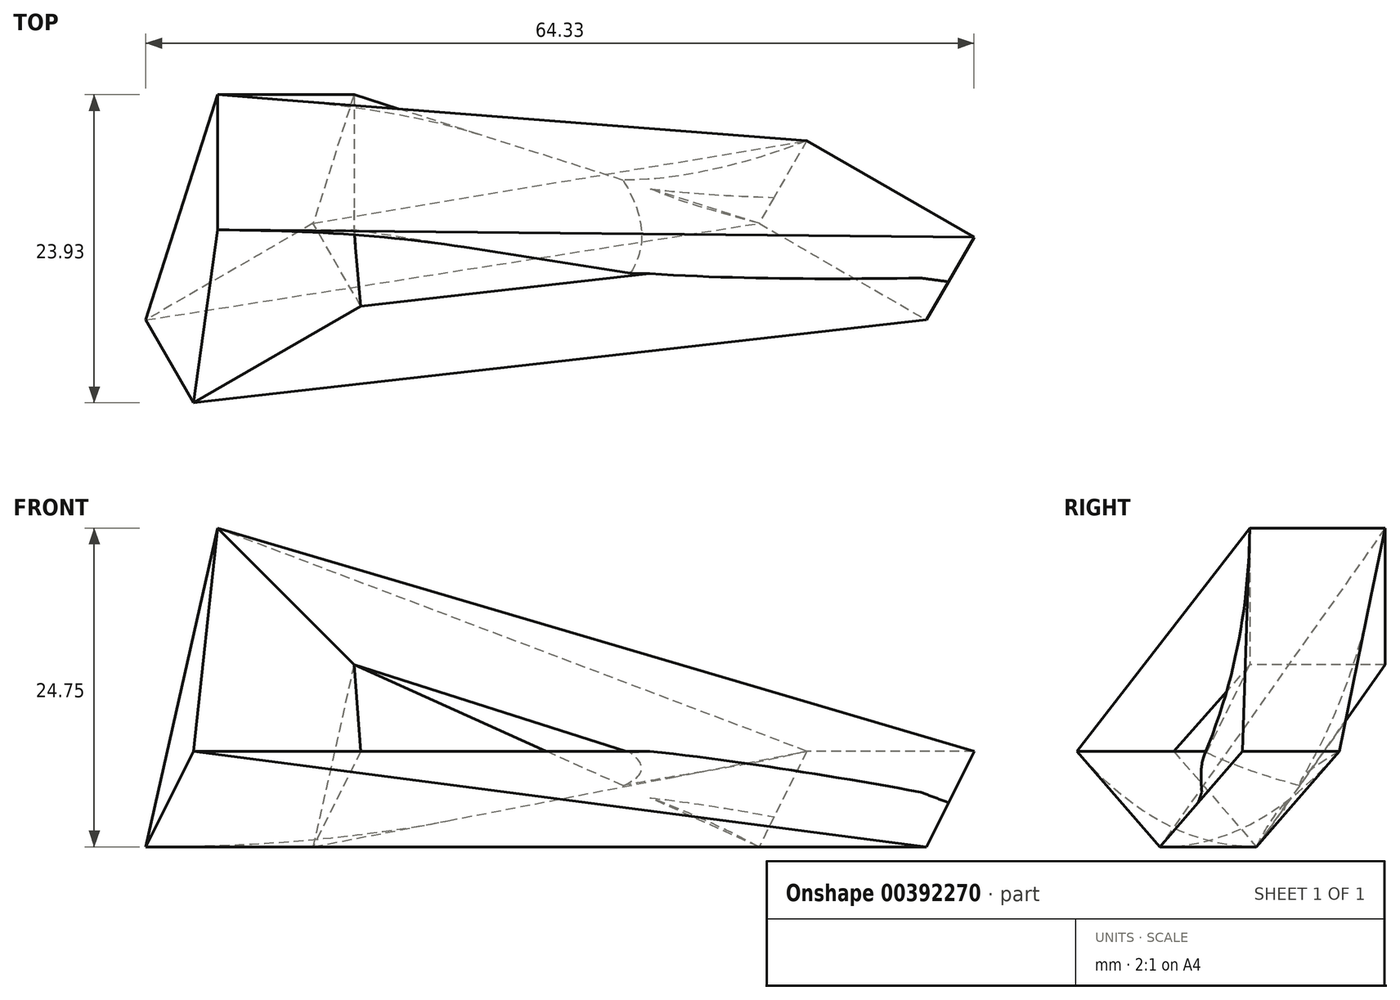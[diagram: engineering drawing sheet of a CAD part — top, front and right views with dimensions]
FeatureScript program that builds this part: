
annotation { "Feature Type Name" : "Feature", "Feature Type Description" : "" }
export const myFeature = defineFeature(function(context is Context, id is Id, definition is map)
    precondition{}
    {
        {
            var Q0;
            Q0=qCreatedBy(makeId("Top.planeOp"),FACE);
            var sketch = newSketch(context, id + "F0", { "sketchPlane" : qUnion([Q0])});
            skLineSegment(sketch, "E0", {"start": v(0, 0) * mm, "end": v(0, 80) * mm, "construction": true});
            skLineSegment(sketch, "E1", {"start": v(0, 0) * mm, "end": v(69.28, -40) * mm, "construction": true});
            skLineSegment(sketch, "E2", {"start": v(0, 0) * mm, "end": v(-69.28, -40) * mm, "construction": true});
            skSolve(sketch);
        }
        {
            var Q0;
            Q0=sQuery(id+"F0.wireOp",EDGE,"E0");
            cPlane(context, id + "F1", {"entities" : qUnion([Q0]), "cplaneType" : CPlaneType.LINE_ANGLE, "offset" : 25 * mm, "angle" : 45 * degree, "width" : 150 * mm, "height" : 150 * mm});
        }
        {
            var Q0;
            Q0=qCreatedBy(id+"F1.planeOp",FACE);
            var sketch = newSketch(context, id + "F2", { "sketchPlane" : qUnion([Q0])});
            skLineSegment(sketch, "E3.bottom", {"start": v(0, 35) * mm, "end": v(-10.5, 35) * mm});
            skLineSegment(sketch, "E3.top", {"start": v(0, 20) * mm, "end": v(-10.5, 20) * mm});
            skLineSegment(sketch, "E3.left", {"start": v(0, 35) * mm, "end": v(0, 20) * mm});
            skLineSegment(sketch, "E3.right", {"start": v(-10.5, 35) * mm, "end": v(-10.5, 20) * mm});
            skSolve(sketch);
        }
        {
            var Q0;
            Q0=sQuery(id+"F0.wireOp",EDGE,"E2");
            cPlane(context, id + "F3", {"entities" : qUnion([Q0]), "cplaneType" : CPlaneType.LINE_ANGLE, "offset" : 25 * mm, "angle" : 45 * degree, "oppositeDirection" : true, "width" : 150 * mm, "height" : 150 * mm});
        }
        {
            var Q0;
            Q0=qCreatedBy(id+"F3.planeOp",FACE);
            var sketch = newSketch(context, id + "F4", { "sketchPlane" : qUnion([Q0])});
            skLineSegment(sketch, "E4.0", {"start": v(0, 0) * mm, "end": v(-74.07, 30.24) * mm, "construction": true});
            skLineSegment(sketch, "E5", {"start": v(-32.4, 13.23) * mm, "end": v(-18.52, 7.56) * mm, "construction": true});
            skLineSegment(sketch, "E6", {"start": v(-14.55, 17.28) * mm, "end": v(-18.52, 7.56) * mm});
            skLineSegment(sketch, "E7", {"start": v(-14.55, 17.28) * mm, "end": v(-28.44, 22.95) * mm});
            skLineSegment(sketch, "E8", {"start": v(-32.4, 13.23) * mm, "end": v(-28.44, 22.95) * mm});
            skLineSegment(sketch, "E9", {"start": v(-18.52, 7.56) * mm, "end": v(-32.4, 13.23) * mm});
            skSolve(sketch);
        }
        {
            var Q0;
            Q0=sQuery(id+"F0.wireOp",EDGE,"E1");
            cPlane(context, id + "F5", {"entities" : qUnion([Q0]), "cplaneType" : CPlaneType.LINE_ANGLE, "offset" : 25 * mm, "angle" : 45 * degree, "oppositeDirection" : true, "width" : 150 * mm, "height" : 150 * mm});
        }
        {
            var Q0;
            Q0=qCreatedBy(id+"F5.planeOp",FACE);
            var sketch = newSketch(context, id + "F6", { "sketchPlane" : qUnion([Q0])});
            skLineSegment(sketch, "E10.0", {"start": v(0, 0) * mm, "end": v(74.07, 30.24) * mm, "construction": true});
            skLineSegment(sketch, "E11", {"start": v(18.52, 7.56) * mm, "end": v(32.4, 13.23) * mm});
            skLineSegment(sketch, "E12", {"start": v(32.4, 13.23) * mm, "end": v(36.37, 3.5) * mm});
            skLineSegment(sketch, "E13", {"start": v(36.37, 3.5) * mm, "end": v(22.49, -2.16) * mm});
            skLineSegment(sketch, "E14", {"start": v(22.49, -2.16) * mm, "end": v(18.52, 7.56) * mm});
            skSolve(sketch);
        }
        {
            var Q0;
            Q0=makeQuery(id+"F2.imprint","IMPRINT",FACE,{"disambiguationData":[TD([[makeQuery(id+"F2.imprint","IMPRINT",EDGE,{"derivedFrom":sQuery(id+"F2.wireOp",EDGE,"E3.bottom")}),1.0]])]});
            var Q1;
            Q1=makeQuery(id+"F4.imprint","IMPRINT",FACE,{"disambiguationData":[TD([[makeQuery(id+"F4.imprint","IMPRINT",EDGE,{"derivedFrom":sQuery(id+"F4.wireOp",EDGE,"E6")}),-1.0]])]});
            loft(context, id + "F7", {"sheetProfilesArray" : [{ "sheetProfileEntities" : qUnion([Q0]) }, { "sheetProfileEntities" : qUnion([Q1]) }]});
        }
        {
            var Q1;
            Q1=makeQuery(id+"F7.opLoft","CAP_FACE",FACE,{"disambiguationData":[OSD([makeQuery(id+"F4.imprint","IMPRINT",FACE,{"disambiguationData":[TD([[makeQuery(id+"F4.imprint","IMPRINT",EDGE,{"derivedFrom":sQuery(id+"F4.wireOp",EDGE,"E6")}),-1.0]])]})])],"isStart":true});
            var Q2;
            Q2=makeQuery(id+"F6.imprint","IMPRINT",FACE,{"disambiguationData":[TD([[makeQuery(id+"F6.imprint","IMPRINT",EDGE,{"derivedFrom":sQuery(id+"F6.wireOp",EDGE,"E11")}),-1.0]])]});
            loft(context, id + "F8", {"operationType" : NewBodyOperationType.ADD, "sheetProfilesArray" : [{ "sheetProfileEntities" : qUnion([Q1]) }, { "sheetProfileEntities" : qUnion([Q2]) }]});
        }
        {
            var Q1;
            Q1=makeQuery(id+"F8.opLoft","CAP_FACE",FACE,{"disambiguationData":[OSD([makeQuery(id+"F6.imprint","IMPRINT",FACE,{"disambiguationData":[TD([[makeQuery(id+"F6.imprint","IMPRINT",EDGE,{"derivedFrom":sQuery(id+"F6.wireOp",EDGE,"E11")}),-1.0]])]})])],"isStart":true});
            var Q2;
            Q2=makeQuery(id+"F7.opLoft","CAP_FACE",FACE,{"disambiguationData":[OSD([makeQuery(id+"F2.imprint","IMPRINT",FACE,{"disambiguationData":[TD([[makeQuery(id+"F2.imprint","IMPRINT",EDGE,{"derivedFrom":sQuery(id+"F2.wireOp",EDGE,"E3.bottom")}),1.0]])]})])],"isStart":true});
            loft(context, id + "F9", {"operationType" : NewBodyOperationType.ADD, "sheetProfilesArray" : [{ "sheetProfileEntities" : qUnion([Q1]) }, { "sheetProfileEntities" : qUnion([Q2]) }]});
        }
    });
